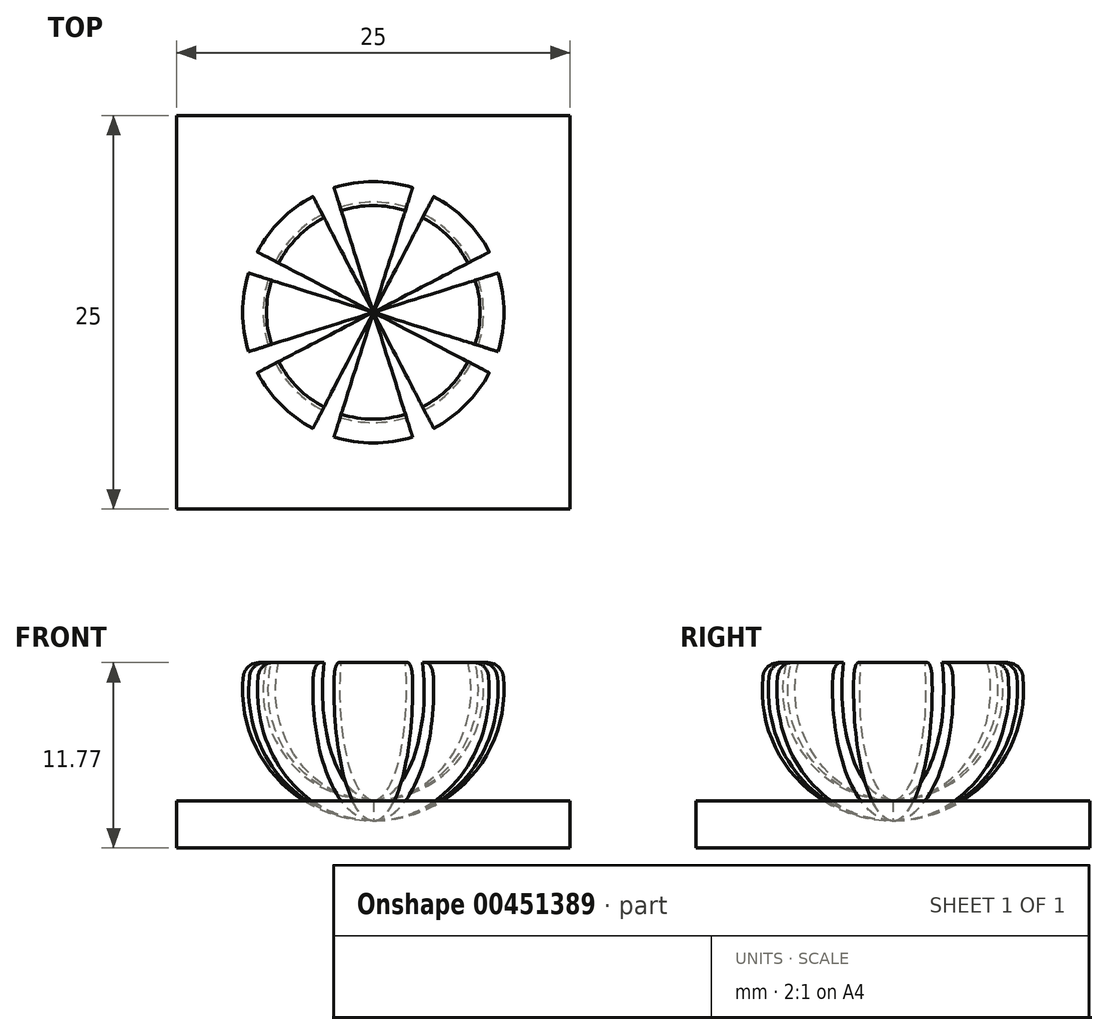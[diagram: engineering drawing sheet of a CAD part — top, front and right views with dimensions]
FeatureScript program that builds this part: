
annotation { "Feature Type Name" : "Feature", "Feature Type Description" : "" }
export const myFeature = defineFeature(function(context is Context, id is Id, definition is map)
    precondition{}
    {
        {
            var Q0;
            Q0=qCreatedBy(makeId("Top.planeOp"),FACE);
            var sketch = newSketch(context, id + "F0", { "sketchPlane" : qUnion([Q0])});
            skLineSegment(sketch, "E0.bottom", {"start": v(-12.5, -12.5) * mm, "end": v(12.5, -12.5) * mm});
            skLineSegment(sketch, "E0.top", {"start": v(-12.5, 12.5) * mm, "end": v(12.5, 12.5) * mm});
            skLineSegment(sketch, "E0.left", {"start": v(-12.5, -12.5) * mm, "end": v(-12.5, 12.5) * mm});
            skLineSegment(sketch, "E0.right", {"start": v(12.5, -12.5) * mm, "end": v(12.5, 12.5) * mm});
            skPoint(sketch, "E0.middle", {"position": v(0, 0) * mm});
            skSolve(sketch);
        }
        {
            var Q0;
            Q0=makeQuery(id+"F0.imprint","IMPRINT",FACE,{"disambiguationData":[TD([[makeQuery(id+"F0.imprint","IMPRINT",EDGE,{"derivedFrom":sQuery(id+"F0.wireOp",EDGE,"E0.bottom")}),1.0]])]});
            extrude(context, id + "F1", {"entities" : qUnion([Q0]), "depth" : 3 * mm});
        }
        {
            var Q0;
            Q0=qCreatedBy(makeId("Front.planeOp"),FACE);
            var sketch = newSketch(context, id + "F2", { "sketchPlane" : qUnion([Q0])});
            skArc(sketch, "E1", {"start": v(0, 3.03) * mm, "mid": v(5.53, 5.74) * mm, "end": v(6.78, 11.77) * mm});
            skArc(sketch, "E2", {"start": v(0, 1.73) * mm, "mid": v(6.16, 4.47) * mm, "end": v(8.26, 10.88) * mm});
            skLineSegment(sketch, "E3", {"start": v(6.78, 11.77) * mm, "end": v(7.26, 11.77) * mm});
            skLineSegment(sketch, "E4", {"start": v(0, 3.03) * mm, "end": v(0, 1.73) * mm});
            skPoint(sketch, "E5.visualSharp", {"position": v(8.11, 11.77) * mm});
            skArc(sketch, "E5.filletArc", {"start": v(8.26, 10.88) * mm, "mid": v(7.93, 11.52) * mm, "end": v(7.26, 11.77) * mm});
            skLineSegment(sketch, "E6", {"start": v(0, 12.56) * mm, "end": v(0, -1.82) * mm, "construction": true});
            skSolve(sketch);
        }
        {
            var Q0;
            Q0=makeQuery(id+"F2.imprint","IMPRINT",FACE,{"disambiguationData":[TD([[makeQuery(id+"F2.imprint","IMPRINT",EDGE,{"derivedFrom":sQuery(id+"F2.wireOp",EDGE,"E1")}),-1.0]])]});
            var Q1;
            Q1=sQuery(id+"F2.wireOp",EDGE,"E6");
            revolve(context, id + "F3", {"entities" : qUnion([Q0]), "axis" : qUnion([Q1]), "revolveType" : RevolveType.SYMMETRIC, "angle" : 35 * degree});
        }
        {
            var Q0;
            Q0=makeQuery(id+"F3.opRevolve","SWEPT_BODY",BODY,{"disambiguationData":[OSD([sQuery(id+"F2.wireOp",EDGE,"E1"),sQuery(id+"F2.wireOp",EDGE,"E2"),sQuery(id+"F2.wireOp",EDGE,"E3"),sQuery(id+"F2.wireOp",EDGE,"E4"),sQuery(id+"F2.wireOp",EDGE,"E5.filletArc")])]});
            var Q1;
            Q1=sQuery(id+"F2.wireOp",EDGE,"E6");
            circularPattern(context, id + "F4", {"entities" : qUnion([Q0]), "axis" : qUnion([Q1]), "angle" : 360 * degree, "instanceCount" : 8, "equalSpace" : true});
        }
    });
